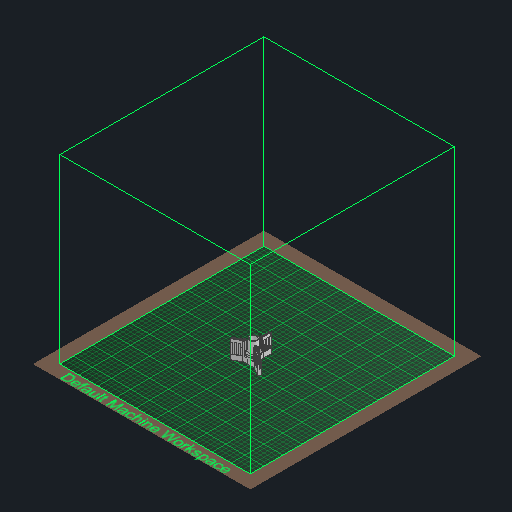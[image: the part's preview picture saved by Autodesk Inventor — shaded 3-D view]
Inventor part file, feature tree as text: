
AUTODESK INVENTOR PART (.ipt)
format: ipt  version: 2022 (Build 260153000, 153)  size: 963,584 bytes
history: native  units: in
note: dims shown in document units (in); Inventor stores cm internally (conversion verified against a paired STEP export)
features: projected_geometry x17, sketch x15, extrude x13, pattern_circular x2, chamfer x1, pattern_linear x1, plane x1, fillet x1
ambient origin geometry x8: Origin, YZ Plane, XZ Plane, XY Plane, X Axis, Y Axis, Z Axis, Center Point
bodies: Solid1 (feature_tree)
feature tree (51):
  extrude  "Extrusion1"  Depth=0.55in
  extrude  "Extrusion2"  Depth=0.125in TaperAngle=0.0deg
  extrude  "Extrusion3"  Depth=0.375in TaperAngle=0.0deg
  extrude  "Extrusion4"  Depth=0.15in
  sketch  "Sketch5"  dims[d11=0.0in d12=1.0in d13=0.0in]
  extrude  "Extrusion5"  Depth=1.0in TaperAngle=0.0deg
  chamfer  "Chamfer1"  Distance=1.0in
  sketch  "Sketch7"  dims[d17=0.08in d18=0.125in d19=45.0deg d20=1.0in]
  extrude  "Extrusion7"  Depth=1.0in
  extrude  "Extrusion8"  Depth=0.25in TaperAngle=0.0deg
  pattern_linear  "Rectangular Pattern1"  Count1=4 Spacing1=0.25in
  plane  "Work Plane1"
  fillet  "Fillet1"  Radius=0.5in
  pattern_circular  "Circular Pattern1"  Count=3 Angle=360.0deg
  extrude  "Extrusion10"  Depth=0.25in TaperAngle=0.0deg
  extrude  "Extrusion11"  Depth=0.125in
  extrude  "Extrusion12"  Depth=0.15in TaperAngle=360.0deg
  extrude  "Extrusion13"  Depth=0.25in TaperAngle=0.0deg
  sketch  "Sketch14"  dims[d56=0.3in d57=0.0in d58=0.25in d59=0.0in]
  pattern_circular  "Circular Pattern3"  [2 undecoded]
  extrude  "Extrusion14"  [1 undecoded]
  extrude  "Extrusion15"  [1 undecoded]
  sketch  "Sketch1"  dims[d0=0.69in d1=0.55in]
  sketch  "Sketch2"  dims[d2=1.0in d3=0.0in d4=0.125in d5=0.0in]
  sketch  "Sketch3"  dims[d6=0.875in d7=0.375in d8=0.0in]
  sketch  "Sketch4"  dims[d9=1.4375in d10=0.15in]
  projected_geometry  "Projected Loop1"
  sketch  "Sketch6"  dims[d14=0.0714in d15=1.0in d16=0.0in]
  projected_geometry  "Projected Loop2"
  sketch  "Sketch8"  dims[d23=0.25in d24=0.125in d25=0.0in]
  projected_geometry  "Projected Loop3"
  sketch  "Sketch9"  dims[d26=0.125in d27=0.0in d28=1.5748in d30=0.25in d37=0.5in d38=1.1811in d39=360.0deg]
  projected_geometry  "Projected Loop4"
  projected_geometry  "Projected Loop5"
  sketch  "Sketch11"  dims[d41=0.05in d42=0.0in d43=0.25in d44=0.0in]
  projected_geometry  "Projected Loop6"
  sketch  "Sketch12"  dims[d45=0.125in d46=0.0in d47=0.125in]
  projected_geometry  "Projected Loop7"
  projected_geometry  "Projected Loop8"
  projected_geometry  "Projected Loop9"
  projected_geometry  "Projected Loop10"
  projected_geometry  "Projected Loop11"
  projected_geometry  "Projected Loop12"
  sketch  "Sketch13"  dims[d48=0.15in d49=0.0in d53=1.1811in d54=360.0deg]
  projected_geometry  "Projected Loop13"
  sketch  "Sketch15"
  projected_geometry  "Projected Loop14"
  projected_geometry  "Projected Loop15"
  projected_geometry  "Projected Loop16"
  sketch  "Sketch16"
  projected_geometry  "Projected Loop17"
note: 4 required parameter values undecoded (feature->parameter linkage not recoverable at this tier; creation-order binding heuristic only, values carry confidence <= 0.55)
